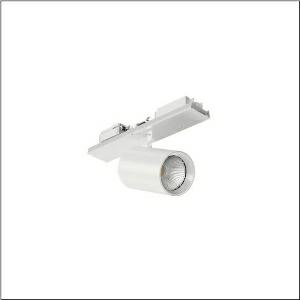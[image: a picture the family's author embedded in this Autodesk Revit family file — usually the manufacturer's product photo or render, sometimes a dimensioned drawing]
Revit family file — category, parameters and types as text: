
# Revit family: licross_r__spot_31_51sl147a45b_9b2d
name_source: partatom
category: Lighting Fixtures
units: mm (PartAtom-declared; Revit-internal decimal feet)

## family parameters
Cut with Voids When Loaded = No
Host = Face
Light Source = No
Part Type = Normal
Room Calculation Point = No
Round Connector Dimension = Use Diameter
Shared = No

## types (1)
- --- (1 x LED, 5250 lm, 42.4 W, 4000K)
    Apparent Load = 42 VA
    CIE Flux Codes = 93 97 100 100 100
    Color Rendering = 90
    Color Temperature = 4000K
    Default Elevation = 1800 mm
    Description = Licross® Spot 31, directional spotlight, light control with lens, of plastic, LED rated luminous flux: 5.250lm, light colour: 940, with plug, 3-pole, with phase selection, mains connection: 220..240V, AC, 50/60Hz, of aluminium, traffic white (RAL 9016), length: 300mm, diameter: 90mm, protection rating (complete): IP20, insulation class (complete): insulation class I (protective earthing), certification: CE, packaging unit: 1 piece
    Height = 175 mm
    Lamp = 1 x LED
    Lamp Light Flux = 5250 lm
    Lamp Power = 42.4 W
    Lamp count = 1
    Length = 90 mm
    Luminous efficacy = 124 lm/W
    Manufacturer = Siteco
    ModVariant = No
    Model = 51SL147A45B
    Mounting Place = Ceiling
    Mounting Type = Pendant
    Number of Poles = 1
    OnlyDefault = Yes
    Power Factor = 1
    Product Name = Licross® Spot 31
    Product group = directional spotlight
    ProductGroupID = 906
    Protection Class = Protection class I
    Protection Degree = IP 20
    RLX_Detail_Level = 1
    RLX_Emergency_Light_Flux = 0 lm
    RLX_Emergency_Type = 0
    RLX_Emergency_Type_DB = No
    RlxData = <blob elided: 14793 chars, md5=497b2f00>
    Socket = socket
    Standby Power = 0 W
    System Light Flux = 5250 lm
    System Power = 42 W
    Type Comments = factory setting: luminous flux: 100 % | (ON | ON | ON) | 1050 mA
    Type Image = l_1245720.jpg
    URL = http://relux.com
    VarID = @adj_131944
    Voltage = 0 V
    Weight = 0.00 kg
    Width = 0 mm  [stored 0 ft]

note: [stored X ft] marks values corroborated as IEEE doubles in the binary element streams (Revit-internal decimal feet)

## geometry (parser evidence)
native form markers: Sweep x12
no freeform markers — native parametric forms only
